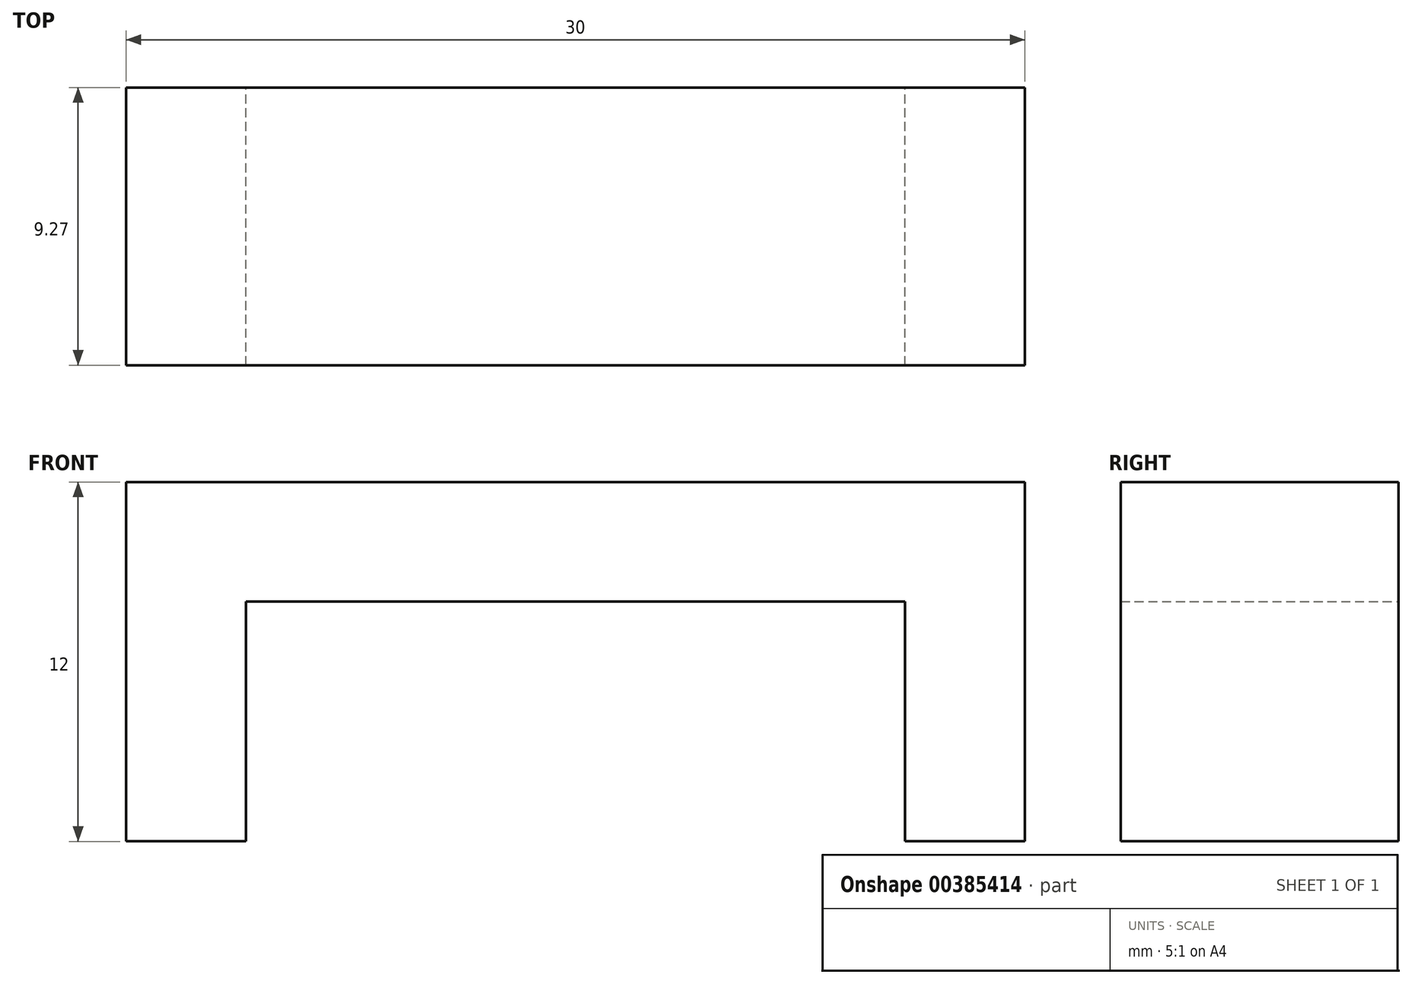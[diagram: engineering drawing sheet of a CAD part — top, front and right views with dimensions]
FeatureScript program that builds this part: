
annotation { "Feature Type Name" : "Feature", "Feature Type Description" : "" }
export const myFeature = defineFeature(function(context is Context, id is Id, definition is map)
    precondition{}
    {
        {
            var Q0;
            Q0=qCreatedBy(makeId("Front.planeOp"),FACE);
            var sketch = newSketch(context, id + "F0", { "sketchPlane" : qUnion([Q0])});
            skLineSegment(sketch, "E0", {"start": v(-9.6, 22.34) * mm, "end": v(12.4, 22.34) * mm});
            skLineSegment(sketch, "E1", {"start": v(12.4, 22.34) * mm, "end": v(12.4, 14.34) * mm});
            skLineSegment(sketch, "E2", {"start": v(12.4, 14.34) * mm, "end": v(16.4, 14.34) * mm});
            skLineSegment(sketch, "E3", {"start": v(16.4, 14.34) * mm, "end": v(16.4, 26.34) * mm});
            skLineSegment(sketch, "E4", {"start": v(16.4, 26.34) * mm, "end": v(-13.6, 26.34) * mm});
            skLineSegment(sketch, "E5", {"start": v(-13.6, 26.34) * mm, "end": v(-13.6, 14.34) * mm});
            skLineSegment(sketch, "E6", {"start": v(-13.6, 14.34) * mm, "end": v(-9.6, 14.34) * mm});
            skLineSegment(sketch, "E7", {"start": v(-9.6, 14.34) * mm, "end": v(-9.6, 22.34) * mm});
            skSolve(sketch);
        }
        {
            var Q0;
            Q0=makeQuery(id+"F0.imprint","IMPRINT",FACE,{"disambiguationData":[TD([[makeQuery(id+"F0.imprint","IMPRINT",EDGE,{"derivedFrom":sQuery(id+"F0.wireOp",EDGE,"E0")}),1.0]])]});
            extrude(context, id + "F1", {"entities" : qUnion([Q0]), "depth" : 9.27 * mm});
        }
    });
